# Revit family: 0059827 Feilo Sylvania Lighting Fixture SYLFIRE LED G2 WH TLT WW DIM DC
name_source: partatom
category: Lighting Fixtures
revit_build: Autodesk Revit 2017 (Build: 20190507_1515(x64)
units: mm (PartAtom-declared; Revit-internal decimal feet)

## family parameters
Cut with Voids When Loaded = No
Host = Face
Light Source = No
OmniClass Number = 23.80.70.00
OmniClass Title = Lighting
Part Type = Normal
Room Calculation Point = No
Round Connector Dimension = Use Diameter
Shared = No

## types (1)
- 0059827 SYLFIRE LED G2 WH TLT WW DIM DC
    Apparent Load = 8 VA
    Assembly Code = D5020200
    AssetType = Fixed
    ClassificationName = Uniclass2015
    ClassificationValue = EF_70_80
    Cost = 0 $
    Default Elevation = 1219 mm
    Description = IP20 LED downlight, fire rated for 30, 60 and 90 minutes. 8W up to 620 lumen output.
    DimmingControlOptions = Non dimmable
    DocumentationLiterature = http://www.sylvania-lighting.com
    DurationUnit = hours
    ElectricShockClassification = Class II
    EndAngle_FEILO = 180.00°
    ExpectedLife = 50000
    IfcExportAs = IfcLightFixtureType
    IfcExportType = IfcLightFixtureType
    ImpactProtectionIndex = IK06
    IngressProtection = IP20
    InputNominalFrequency = 50/60 Hz
    InputVoltage = 220-240V~
    Keynote = 16500
    Lamp = LED
    LampColourRenderingIndex = 80
    LampColourTemperature = 3000 K
    LampNominalLuminous = 600 lm
    LampsType = LED
    LuminousEfficacy = 75 lm/W
    Manufacturer = Feilo Sylvania
    ManufacturerName = Feilo Sylvania
    Material_1_FEILO = Body-Sylvania-SylFire-White
    Material_2_FEILO = LED-Sylvania-SylFire
    Material_3_FEILO = <By Category>
    Material_4_FEILO = <By Category>
    Model = SYLFIRE LED G2 WH TLT WW DIM DC
    ModelNumber = 0059827
    ModelReference = SYLFIRE LED G2 WH TLT WW DIM DC
    Name = SYLFIRE LED G2 WH TLT WW DIM DC
    NominalDepth = 92 mm
    NominalHeight = 117 mm
    NominalLength = 92 mm
    PowerConsumption = 8 W
    PowerFactor = 0.85
    TiltAngle_FEILO = 0.00°
    Type Image = <None>
    TypeHead_FEILO = SylFire Tiltable Head : 0059827 SYLFIRE LED G2 WH TLT WW DIM DC
    TypeName = SYLFIRE LED G2 WH TLT WW DIM DC
    URL = http://www.sylvania-lighting.com
    Voltage = 230 V
    Weight = 9.58 kg

## geometry (parser evidence)
native form markers: Sweep x4
no freeform markers — native parametric forms only
